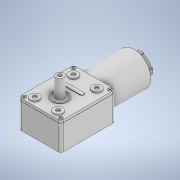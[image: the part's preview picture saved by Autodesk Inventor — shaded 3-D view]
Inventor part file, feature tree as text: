
AUTODESK INVENTOR PART (.ipt)
format: ipt  version: 2021 (Build 250183000, 183)  size: 424,960 bytes
history: native  units: mm
features: sketch x24, extrude x21, fillet x6, other x1
ambient origin geometry x8: Origin, YZ Plane, XZ Plane, XY Plane, X Axis, Y Axis, Z Axis, Center Point
bodies: Body1 (feature_tree), Body2 (feature_tree)
feature tree (52):
  other  "Sólido1"
  extrude  "Extrusión1"  Depth=31.5mm
  extrude  "Extrusión2"  Depth=33.0mm TaperAngle=0.0deg
  sketch  "Boceto3"  dims[d15=6.0mm d16=0.0mm d17=2.0mm]
  extrude  "Extrusión3"  Depth=2.0mm
  extrude  "Extrusión4"  Depth=5.0mm TaperAngle=0.0deg
  extrude  "Extrusión5"  Depth=3.0mm
  extrude  "Extrusión6"  Depth=4.0mm TaperAngle=0.0deg
  extrude  "Extrusión7"  Depth=3.0mm TaperAngle=0.0deg
  extrude  "Extrusión8"  Depth=2.0mm TaperAngle=0.0deg
  extrude  "Extrusión9"  Depth=2.0mm
  sketch  "Boceto11"  dims[d95=2.0mm d96=0.0mm d97=0.1mm]
  fillet  "Empalme1"  Radius=2.0mm
  fillet  "Empalme2"  Radius=2.0mm
  fillet  "Empalme3"  Radius=2.0mm
  fillet  "Empalme4"  Radius=2.0mm
  fillet  "Empalme5"  Radius=2.0mm
  extrude  "Extrusión10"  Depth=2.0mm TaperAngle=0.0deg
  extrude  "Extrusión11"  Depth=2.0mm
  extrude  "Extrusión12"  Depth=2.0mm TaperAngle=0.0deg
  extrude  "Extrusión13"  Depth=10.0mm
  sketch  "Boceto16"  dims[d132=0.4mm d133=0.0mm d134=0.123mm]
  extrude  "Extrusión14"  Depth=0.3mm TaperAngle=0.0deg
  extrude  "Extrusión15"  Depth=13.0mm TaperAngle=0.0deg
  extrude  "Extrusión16"  Depth=0.123mm
  extrude  "Extrusión17"  Depth=0.05mm
  extrude  "Extrusión18"  [1 undecoded]
  extrude  "Extrusión19"  [1 undecoded]
  extrude  "Extrusión20"  [1 undecoded]
  fillet  "Empalme6"  [1 undecoded]
  extrude  "Extrusión21"  [1 undecoded]
  sketch  "Boceto1"  dims[d0=41.0mm d1=31.5mm]
  sketch  "Boceto2"  dims[d2=21.0mm d3=0.0mm d11=33.0mm d12=0.0mm]
  sketch  "Boceto4"  dims[d18=1.0mm d19=0.0mm d26=5.0mm d27=0.0mm]
  sketch  "Boceto5"  dims[d30=4.0mm d31=3.0mm]
  sketch  "Boceto6"  dims[d32=4.0mm d33=4.0mm d34=0.0mm]
  sketch  "Boceto7"  dims[d35=1.0mm d49=3.0mm d50=0.0mm]
  sketch  "Boceto8"  dims[d63=5.5mm d64=0.0mm d69=2.0mm d70=0.0mm]
  sketch  "Boceto9"  dims[d71=2.0mm d72=2.0mm d73=2.0mm d74=2.0mm d75=2.0mm d87=2.0mm d88=0.0mm d89=2.0mm]
  sketch  "Boceto10"  dims[d91=2.0mm d92=0.0mm d93=2.0mm d94=0.0mm]
  sketch  "Boceto12"  dims[d98=2.0mm d99=0.0mm d100=2.0mm d101=0.0mm]
  sketch  "Boceto13"  dims[d106=0.3mm d107=0.0mm d110=10.0mm]
  sketch  "Boceto14"  dims[d111=9.9mm d112=0.3mm d113=0.0mm]
  sketch  "Boceto15"  dims[d115=14.0mm d116=0.0mm d118=13.0mm d119=0.0mm]
  sketch  "Boceto17"  dims[d149=0.05mm d150=0.0mm d90=0.872665mm]
  sketch  "Boceto18"
  sketch  "Boceto19"
  sketch  "Boceto20"
  sketch  "Boceto21"
  sketch  "Boceto22"
  sketch  "Boceto23"
  sketch  "Boceto24"
note: 5 required parameter values undecoded (feature->parameter linkage not recoverable at this tier; creation-order binding heuristic only, values carry confidence <= 0.55)
